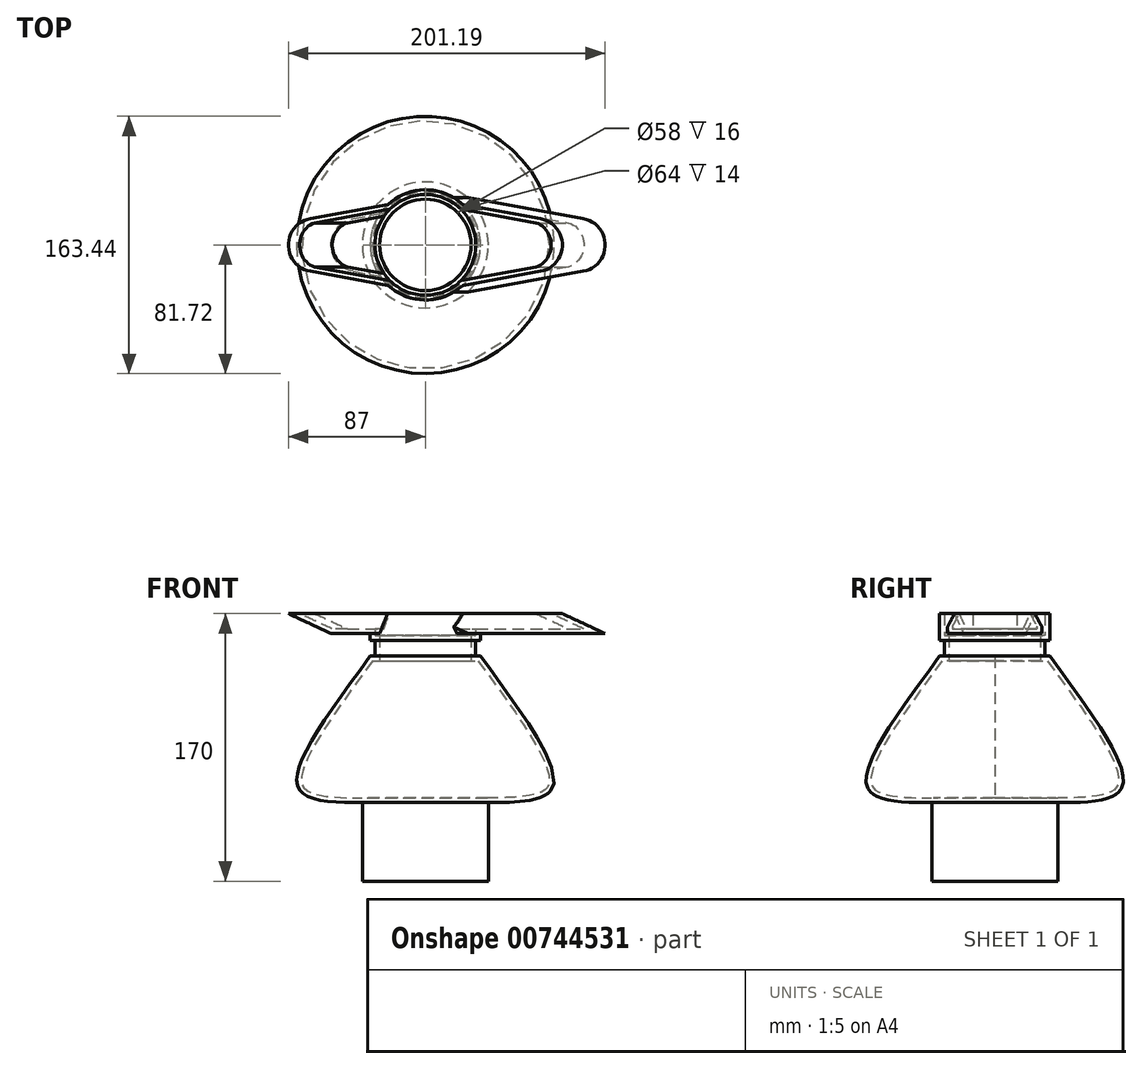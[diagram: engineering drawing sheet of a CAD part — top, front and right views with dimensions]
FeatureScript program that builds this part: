
annotation { "Feature Type Name" : "Feature", "Feature Type Description" : "" }
export const myFeature = defineFeature(function(context is Context, id is Id, definition is map)
    precondition{}
    {
        {
            var Q0;
            Q0=qCreatedBy(makeId("Front.planeOp"),FACE);
            var sketch = newSketch(context, id + "F0", { "sketchPlane" : qUnion([Q0])});
            skLineSegment(sketch, "E0", {"start": v(40, 0) * mm, "end": v(0, 0) * mm});
            skLineSegment(sketch, "E1", {"start": v(0, 0) * mm, "end": v(0, 120) * mm});
            skLineSegment(sketch, "E2", {"start": v(0, 120) * mm, "end": v(35, 120) * mm});
            skLineSegment(sketch, "E3", {"start": v(35, 120) * mm, "end": v(35, 103) * mm});
            skLineSegment(sketch, "E4", {"start": v(35, 103) * mm, "end": v(32, 103) * mm});
            skLineSegment(sketch, "E5", {"start": v(32, 103) * mm, "end": v(32, 93) * mm});
            skLineSegment(sketch, "E6", {"start": v(32, 93) * mm, "end": v(35, 93) * mm});
            skFitSpline(sketch, "E7", {"points": [v(35, 93) * mm, v(80.14, 8.32) * mm, v(40, 0) * mm], "startDerivative": vector(154.37, -209.9) * mm, "endDerivative": vector(-132.15, 0) * mm});
            skSolve(sketch);
        }
        {
            var Q0;
            Q0 = qSketchRegion(id + "F0", true);
            var Q1;
            Q1=sQuery(id+"F0.wireOp",EDGE,"E1");
            revolve(context, id + "F1", {"surfaceOperationType" : NewSurfaceOperationType.NEW, "entities" : qUnion([Q0]), "axis" : qUnion([Q1]), "revolveType" : RevolveType.FULL});
        }
        {
            var Q0;
            Q0=makeQuery(id+"F1.opRevolve","SWEPT_FACE",FACE,{"disambiguationData":[OSD([sQuery(id+"F0.wireOp",EDGE,"E2")])]});
            var sketch = newSketch(context, id + "F2", { "sketchPlane" : qUnion([Q0])});
            skArc(sketch, "E8", {"start": v(-87, 0) * mm, "mid": v(-83.05, -10.9) * mm, "end": v(-73.04, -16.73) * mm});
            skLineSegment(sketch, "E9", {"start": v(-73.04, -16.73) * mm, "end": v(0, -30) * mm});
            skLineSegment(sketch, "E10", {"start": v(0, -30) * mm, "end": v(0, 0) * mm});
            skArc(sketch, "E11.MirrorCS", {"start": v(-87, 0) * mm, "mid": v(-83.05, 10.9) * mm, "end": v(-73.04, 16.73) * mm});
            skLineSegment(sketch, "E12.MirrorCS", {"start": v(-73.04, 16.73) * mm, "end": v(0, 30) * mm});
            skLineSegment(sketch, "E13.MirrorCS", {"start": v(0, 30) * mm, "end": v(0, 0) * mm});
            skArc(sketch, "E14.MirrorCS", {"start": v(87, 0) * mm, "mid": v(83.05, 10.9) * mm, "end": v(73.04, 16.73) * mm});
            skLineSegment(sketch, "E15.MirrorCS", {"start": v(73.04, 16.73) * mm, "end": v(0, 30) * mm});
            skLineSegment(sketch, "E16.MirrorCS", {"start": v(73.04, -16.73) * mm, "end": v(0, -30) * mm});
            skArc(sketch, "E17.MirrorCS", {"start": v(87, 0) * mm, "mid": v(83.05, -10.9) * mm, "end": v(73.04, -16.73) * mm});
            skSolve(sketch);
        }
        {
            var Q0;
            Q0=qCreatedBy(makeId("Front.planeOp"),FACE);
            var sketch = newSketch(context, id + "F3", { "sketchPlane" : qUnion([Q0])});
            skLineSegment(sketch, "E18", {"start": v(0, 120) * mm, "end": v(27.19, 107.32) * mm});
            skSolve(sketch);
        }
        {
            var Q0;
            Q0 = qSketchRegion(id + "F2", true);
            var Q1;
            Q1 = qConstructionFilter(qBodyType(qCreatedBy(id + "F3" ,EDGE), BodyType.WIRE), ConstructionObject.NO);
            sweep(context, id + "F4", {"operationType" : NewBodyOperationType.ADD, "profiles" : qUnion([Q0]), "path" : qUnion([Q1])});
        }
        {
            var Q0;
            Q0=makeQuery(id+"F4.boolean.opBoolean","MERGE",FACE,{"derivedFrom":[makeQuery(id+"F1.opRevolve","SWEPT_FACE",FACE,{"disambiguationData":[OSD([sQuery(id+"F0.wireOp",EDGE,"E2")])]}),makeQuery(id+"F4.opSweep","CAP_FACE",FACE,{"disambiguationData":[OSD([sQuery(id+"F2.wireOp",EDGE,"E8"),sQuery(id+"F2.wireOp",EDGE,"E9"),sQuery(id+"F2.wireOp",EDGE,"E10"),sQuery(id+"F2.wireOp",EDGE,"E11.MirrorCS"),sQuery(id+"F2.wireOp",EDGE,"E12.MirrorCS"),sQuery(id+"F2.wireOp",EDGE,"E13.MirrorCS"),sQuery(id+"F3.wireOp",VERTEX,"E18.start")])],"isStart":true})]});
            shell(context, id + "F5", {"entities" : qUnion([Q0]), "thickness" : 3 * mm});
        }
        {
            var Q0;
            Q0=makeQuery(id+"F1.opRevolve","SWEPT_FACE",FACE,{"disambiguationData":[OSD([sQuery(id+"F0.wireOp",EDGE,"E0")])]});
            extrude(context, id + "F6", {"entities" : qUnion([Q0]), "operationType" : NewBodyOperationType.ADD, "depth" : 50 * mm, "offsetDistance" : 25 * mm});
        }
    });
